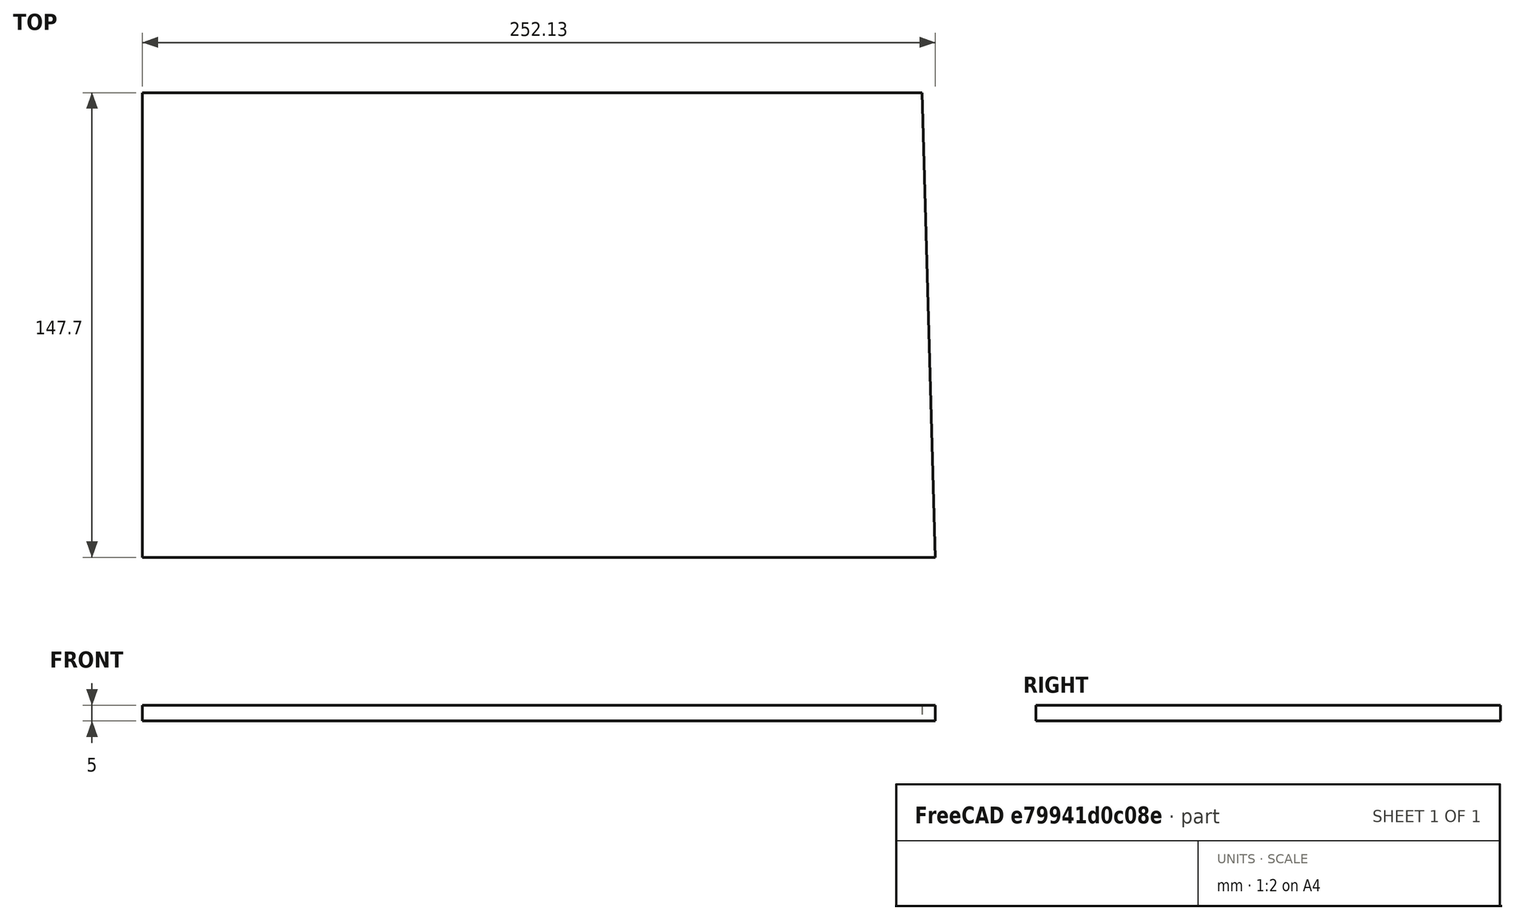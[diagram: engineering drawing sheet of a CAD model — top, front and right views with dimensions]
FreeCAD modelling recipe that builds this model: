
FCSTD DOCUMENT  (FreeCAD 0.19R)
Label: Board Square
License: All rights reserved
LicenseURL: http://en.wikipedia.org/wiki/All_rights_reserved
objects: Sketcher::SketchObject×1, PartDesign::Pad×1, PartDesign::Body×1
note: 4 computed .brp shape members not serialized (recipe doc carries the construction recipe); baked Part::Feature solids carry a one-line shape summary decoded from their .brp

FEATURE [Sketcher::SketchObject] Sketch
  FullyConstrained = false
  MapMode = 5
  Support = -> [XY_Plane]
  sketch-geometry (4):
    g0: LineSegment StartX=0 StartY=20.5475 StartZ=0 EndX=-247.9 EndY=20.5475 EndZ=0
    g1: LineSegment StartX=-247.9 StartY=20.5475 StartZ=0 EndX=-247.9 EndY=-127.148 EndZ=0
    g2: LineSegment StartX=-247.9 StartY=-127.148 StartZ=0 EndX=4.22708 EndY=-127.148 EndZ=0
    g3: LineSegment StartX=4.22708 StartY=-127.148 StartZ=0 EndX=0 EndY=20.5475 EndZ=0
  constraints (8):
    c: PointOnObject(g0,g-2)
    c: Horizontal(g0)
    c: Coincident(g0,g1)
    c: Vertical(g1)
    c: Coincident(g1,g2)
    c: Horizontal(g2)
    c: Coincident(g2,g3)
    c: Coincident(g3,g0)
FEATURE [PartDesign::Pad] Pad  label="Board"
  Direction = (1,1,1)
  Length = 5
  Length2 = 100
  Profile = -> Sketch
  Reversed = true
  Type = 0
FEATURE [PartDesign::Body] Body  label="Board Body"
  Group = -> [Sketch,Pad]
  Origin = -> Origin
  Placement = pos=(247.9,127.148,0) rot=(0,0,1;0rad)
  Tip = -> Pad
